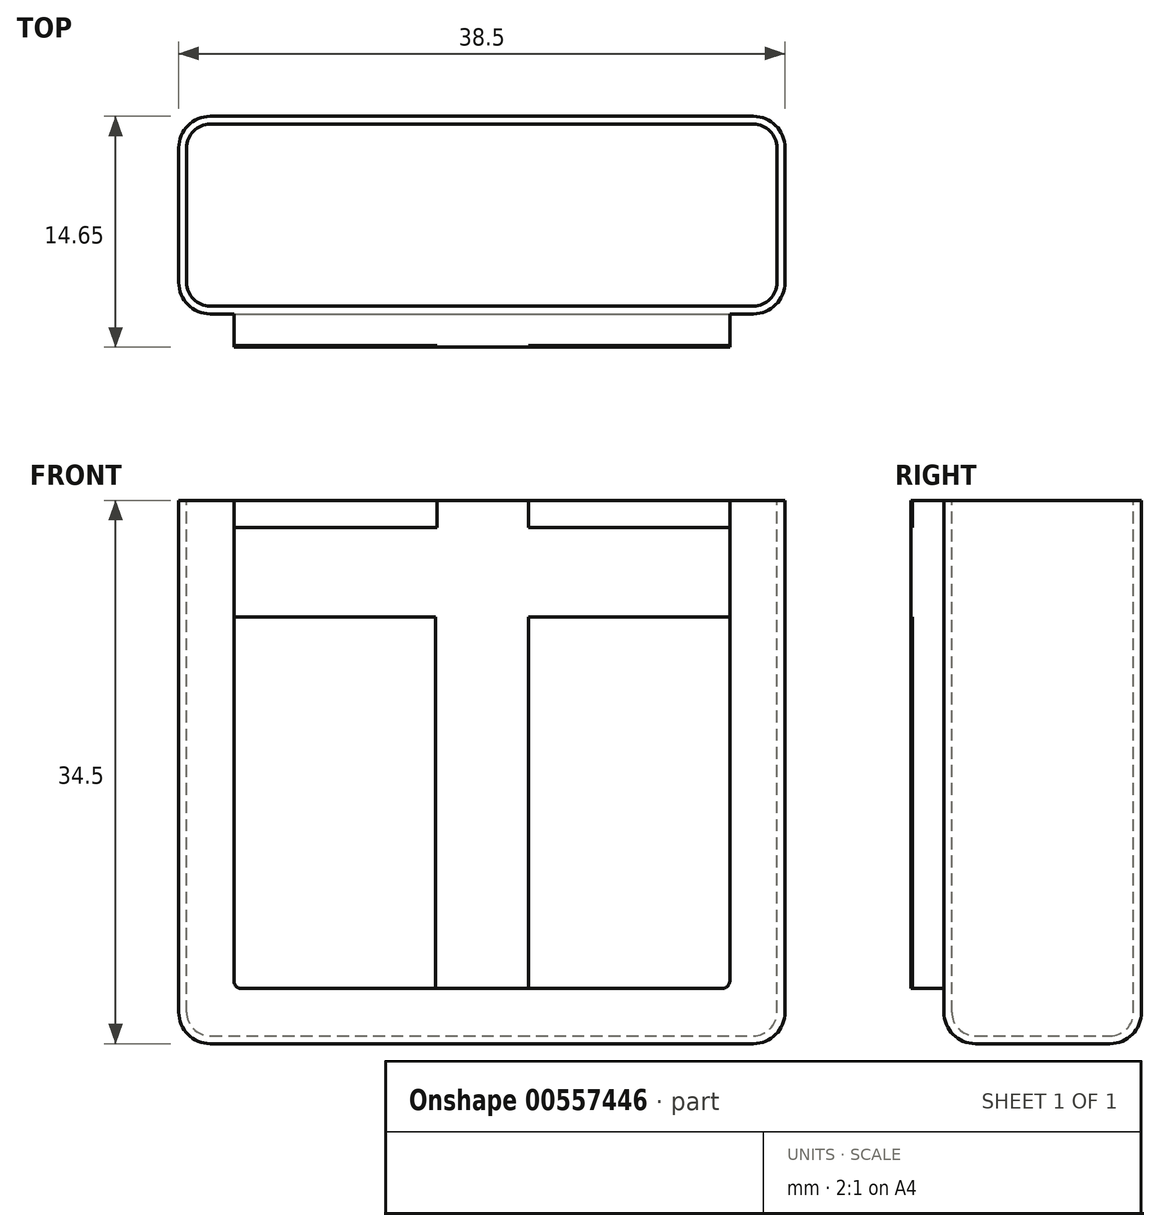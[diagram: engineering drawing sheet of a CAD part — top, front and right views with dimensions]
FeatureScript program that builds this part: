
annotation { "Feature Type Name" : "Feature", "Feature Type Description" : "" }
export const myFeature = defineFeature(function(context is Context, id is Id, definition is map)
    precondition{}
    {
        {
            var Q0;
            Q0=qCreatedBy(makeId("Front.planeOp"),FACE);
            var sketch = newSketch(context, id + "F0", { "sketchPlane" : qUnion([Q0])});
            skLineSegment(sketch, "E0.bottom", {"start": v(-42.14, -23.92) * mm, "end": v(-3.64, -23.92) * mm});
            skLineSegment(sketch, "E0.top", {"start": v(-42.14, 10.58) * mm, "end": v(-3.64, 10.58) * mm});
            skLineSegment(sketch, "E0.left", {"start": v(-42.14, -23.92) * mm, "end": v(-42.14, 10.58) * mm});
            skLineSegment(sketch, "E0.right", {"start": v(-3.64, -23.92) * mm, "end": v(-3.64, 10.58) * mm});
            skLineSegment(sketch, "E1", {"start": v(-47.8, 14.44) * mm, "end": v(-45.89, 12.83) * mm});
            skLineSegment(sketch, "E2.bottom", {"start": v(16, 11.24) * mm, "end": v(54.5, 11.24) * mm});
            skLineSegment(sketch, "E2.top", {"start": v(16, -20.76) * mm, "end": v(54.5, -20.76) * mm});
            skLineSegment(sketch, "E2.left", {"start": v(16, 11.24) * mm, "end": v(16, -20.76) * mm});
            skLineSegment(sketch, "E2.right", {"start": v(54.5, 11.24) * mm, "end": v(54.5, -20.76) * mm});
            skLineSegment(sketch, "E3", {"start": v(9.82, 17.52) * mm, "end": v(9.82, 15.82) * mm});
            skLineSegment(sketch, "E4", {"start": v(13.76, 11.24) * mm, "end": v(13.76, 9.54) * mm});
            skLineSegment(sketch, "E5", {"start": v(13.76, 9.54) * mm, "end": v(16, 9.54) * mm});
            skLineSegment(sketch, "E6.top", {"start": v(-39.52, 10.58) * mm, "end": v(-39.64, 10.58) * mm});
            skLineSegment(sketch, "E7.bottom", {"start": v(-39.64, 10.58) * mm, "end": v(-8.26, 10.58) * mm});
            skSolve(sketch);
        }
        {
            var Q0;
            Q0=makeQuery(id+"F0.imprint","IMPRINT",FACE,{"disambiguationData":[TD([[makeQuery(id+"F0.imprint","IMPRINT",EDGE,{"derivedFrom":sQuery(id+"F0.wireOp",EDGE,"E0.bottom")}),1.0]])]});
            extrude(context, id + "F1", {"entities" : qUnion([Q0]), "depth" : 12.55 * mm, "offsetDistance" : 25 * mm});
        }
        {
            var Q0;
            Q0=makeQuery(id+"F1.opExtrude","CAP_EDGE",EDGE,{"disambiguationData":[OSD([sQuery(id+"F0.wireOp",EDGE,"E0.left")])],"isStart":false});
            var Q1;
            Q1=makeQuery(id+"F1.opExtrude","CAP_EDGE",EDGE,{"disambiguationData":[OSD([sQuery(id+"F0.wireOp",EDGE,"E0.bottom")])],"isStart":false});
            var Q2;
            Q2=makeQuery(id+"F1.opExtrude","CAP_EDGE",EDGE,{"disambiguationData":[OSD([sQuery(id+"F0.wireOp",EDGE,"E0.right")])],"isStart":false});
            fillet(context, id + "F2", {"entities" : qUnion([Q0, Q1, Q2]), "tangentPropagation" : true, "radius" : 2 * mm, "defaultsChanged" : true, "vertexSettings" : [], "allowEdgeOverflow" : false});
        }
        {
            var Q0;
            Q0=makeQuery(id+"F1.opExtrude","CAP_EDGE",EDGE,{"disambiguationData":[OSD([sQuery(id+"F0.wireOp",EDGE,"E0.left")])],"isStart":true});
            var Q1;
            Q1=makeQuery(id+"F1.opExtrude","CAP_EDGE",EDGE,{"disambiguationData":[OSD([sQuery(id+"F0.wireOp",EDGE,"E0.right")])],"isStart":true});
            var Q2;
            Q2=makeQuery(id+"F1.opExtrude","SWEPT_EDGE",EDGE,{"disambiguationData":[OSD([sQuery(id+"F0.wireOp",EDGE,"E0.bottom"),sQuery(id+"F0.wireOp",EDGE,"E0.right")])]});
            var Q3;
            Q3=makeQuery(id+"F1.opExtrude","CAP_EDGE",EDGE,{"disambiguationData":[OSD([sQuery(id+"F0.wireOp",EDGE,"E0.bottom")])],"isStart":true});
            var Q4;
            Q4=makeQuery(id+"F1.opExtrude","SWEPT_EDGE",EDGE,{"disambiguationData":[OSD([sQuery(id+"F0.wireOp",EDGE,"E0.bottom"),sQuery(id+"F0.wireOp",EDGE,"E0.left")])]});
            fillet(context, id + "F3", {"entities" : qUnion([Q0, Q1, Q2, Q3, Q4]), "tangentPropagation" : true, "radius" : 2 * mm, "defaultsChanged" : true, "vertexSettings" : [], "allowEdgeOverflow" : false});
        }
        {
            var Q0;
            Q0=makeQuery(id+"F1.opExtrude","SWEPT_FACE",FACE,{"disambiguationData":[OSD([sQuery(id+"F0.wireOp",EDGE,"E0.top")])]});
            shell(context, id + "F4", {"entities" : qUnion([Q0]), "thickness" : 0.5 * mm});
        }
        {
            var Q0;
            Q0=makeQuery(id+"F1.opExtrude","CAP_FACE",FACE,{"disambiguationData":[OSD([sQuery(id+"F0.wireOp",EDGE,"E0.bottom"),sQuery(id+"F0.wireOp",EDGE,"E0.top"),sQuery(id+"F0.wireOp",EDGE,"E0.left"),sQuery(id+"F0.wireOp",EDGE,"E0.right")])],"isStart":false});
            cPlane(context, id + "F5", {"entities" : qUnion([Q0]), "cplaneType" : CPlaneType.OFFSET, "offset" : 0 * mm, "width" : 150 * mm, "height" : 150 * mm});
        }
        {
            var Q0;
            Q0=qCreatedBy(id+"F5.planeOp",FACE);
            var sketch = newSketch(context, id + "F6", { "sketchPlane" : qUnion([Q0])});
            skLineSegment(sketch, "E8.bottom", {"start": v(-38.64, 10.58) * mm, "end": v(-7.14, 10.58) * mm});
            skLineSegment(sketch, "E8.top", {"start": v(-38.64, -20.42) * mm, "end": v(-7.14, -20.42) * mm});
            skLineSegment(sketch, "E8.left", {"start": v(-38.64, 10.58) * mm, "end": v(-38.64, -20.42) * mm});
            skLineSegment(sketch, "E8.right", {"start": v(-7.14, 10.58) * mm, "end": v(-7.14, -20.42) * mm});
            skSolve(sketch);
        }
        {
            var Q0;
            Q0=makeQuery(id+"F6.imprint","IMPRINT",FACE,{"disambiguationData":[TD([[makeQuery(id+"F6.imprint","IMPRINT",EDGE,{"derivedFrom":sQuery(id+"F6.wireOp",EDGE,"E8.bottom")}),-1.0]])]});
            extrude(context, id + "F7", {"entities" : qUnion([Q0]), "operationType" : NewBodyOperationType.ADD, "depth" : 2 * mm, "offsetDistance" : 25 * mm});
        }
        {
            var Q0;
            Q0=makeQuery(id+"F7.opExtrude","SWEPT_EDGE",EDGE,{"disambiguationData":[OSD([sQuery(id+"F6.wireOp",EDGE,"E8.top"),sQuery(id+"F6.wireOp",EDGE,"E8.left")])]});
            var Q1;
            Q1=makeQuery(id+"F7.opExtrude","SWEPT_EDGE",EDGE,{"disambiguationData":[OSD([sQuery(id+"F6.wireOp",EDGE,"E8.top"),sQuery(id+"F6.wireOp",EDGE,"E8.right")])]});
            fillet(context, id + "F8", {"entities" : qUnion([Q0, Q1]), "tangentPropagation" : true, "radius" : 0.5 * mm, "defaultsChanged" : true, "vertexSettings" : [], "allowEdgeOverflow" : false});
        }
        {
            var Q0;
            Q0=makeQuery(id+"F7.opExtrude","CAP_FACE",FACE,{"disambiguationData":[OSD([sQuery(id+"F6.wireOp",EDGE,"E8.bottom"),sQuery(id+"F6.wireOp",EDGE,"E8.top"),sQuery(id+"F6.wireOp",EDGE,"E8.left"),sQuery(id+"F6.wireOp",EDGE,"E8.right")])],"isStart":false});
            var sketch = newSketch(context, id + "F9", { "sketchPlane" : qUnion([Q0])});
            skLineSegment(sketch, "E9", {"start": v(-38.64, 8.88) * mm, "end": v(-25.72, 8.88) * mm});
            skLineSegment(sketch, "E10", {"start": v(-7.14, 8.88) * mm, "end": v(-19.94, 8.88) * mm});
            skLineSegment(sketch, "E11", {"start": v(-38.64, 8.88) * mm, "end": v(-38.64, 3.18) * mm});
            skLineSegment(sketch, "E12", {"start": v(-38.64, 3.18) * mm, "end": v(-25.84, 3.18) * mm});
            skLineSegment(sketch, "E13", {"start": v(-19.94, 3.18) * mm, "end": v(-7.14, 3.18) * mm});
            skLineSegment(sketch, "E14", {"start": v(-25.72, 8.88) * mm, "end": v(-25.72, 10.58) * mm});
            skLineSegment(sketch, "E15", {"start": v(-19.94, 8.88) * mm, "end": v(-19.94, 10.58) * mm});
            skLineSegment(sketch, "E16", {"start": v(-25.84, 3.18) * mm, "end": v(-25.84, -20.42) * mm});
            skLineSegment(sketch, "E17", {"start": v(-19.94, 3.18) * mm, "end": v(-19.94, -20.42) * mm});
            skSolve(sketch);
        }
        {
            var Q0;
            Q0=makeQuery(id+"F9.imprint","IMPRINT",FACE,{"disambiguationData":[TD([[makeQuery(id+"F9.imprint","IMPRINT",EDGE,{"derivedFrom":sQuery(id+"F9.wireOp",EDGE,"E9")}),-1.0]])]});
            extrude(context, id + "F10", {"entities" : qUnion([Q0]), "operationType" : NewBodyOperationType.ADD, "depth" : 0.1 * mm, "offsetDistance" : 25 * mm});
        }
    });
